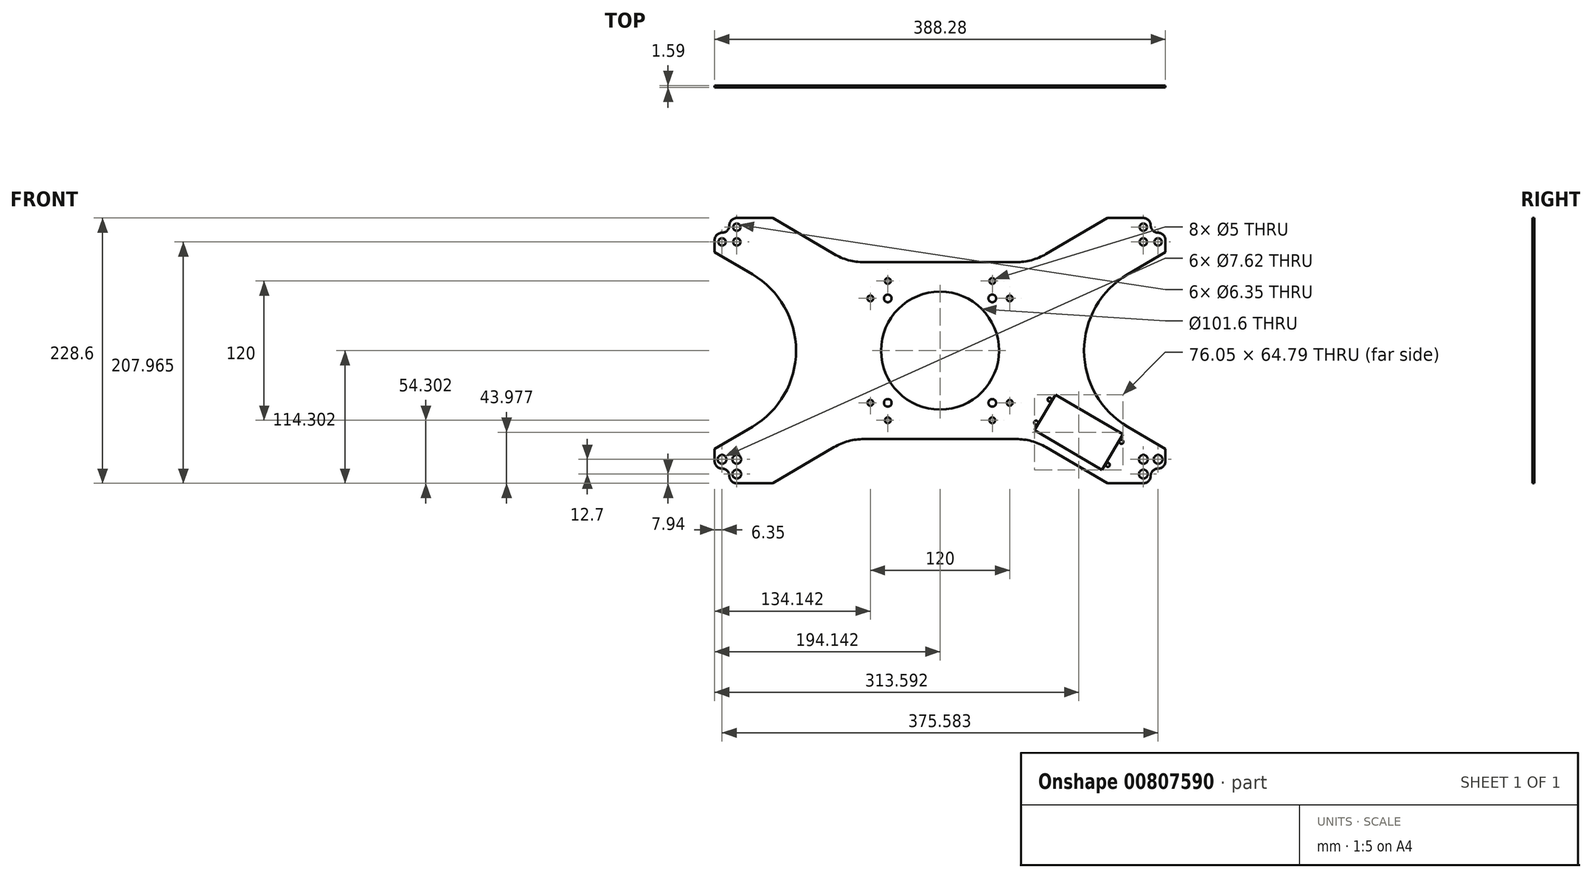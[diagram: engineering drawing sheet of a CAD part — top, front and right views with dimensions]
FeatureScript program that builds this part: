
annotation { "Feature Type Name" : "Feature", "Feature Type Description" : "" }
export const myFeature = defineFeature(function(context is Context, id is Id, definition is map)
    precondition{}
    {
        {
            var Q0;
            Q0=qCreatedBy(makeId("Front.planeOp"),FACE);
            var sketch = newSketch(context, id + "F0", { "sketchPlane" : qUnion([Q0])});
            skCircle(sketch, "E0", {"center": v(0, 0) * mm, "radius": 3.81 * mm});
            skCircle(sketch, "E1", {"center": v(0, 12.7) * mm, "radius": 3.81 * mm});
            skCircle(sketch, "E2", {"center": v(-12.7, 12.7) * mm, "radius": 3.81 * mm});
            skCircle(sketch, "E3", {"center": v(0, 200.03) * mm, "radius": 3.18 * mm});
            skCircle(sketch, "E4", {"center": v(0, 212.73) * mm, "radius": 3.18 * mm});
            skCircle(sketch, "E5", {"center": v(-12.7, 200.03) * mm, "radius": 3.18 * mm});
            skLineSegment(sketch, "E6", {"start": v(175.1, 263.95) * mm, "end": v(175.1, -51.23) * mm, "construction": true});
            skCircle(sketch, "E7.MirrorC", {"center": v(350.18, 212.73) * mm, "radius": 3.18 * mm});
            skCircle(sketch, "E8.MirrorC", {"center": v(362.88, 200.03) * mm, "radius": 3.18 * mm});
            skCircle(sketch, "E9.MirrorC", {"center": v(350.18, 12.7) * mm, "radius": 3.81 * mm});
            skCircle(sketch, "E10.MirrorC", {"center": v(362.88, 12.7) * mm, "radius": 3.81 * mm});
            skCircle(sketch, "E11.MirrorC", {"center": v(350.18, 200.03) * mm, "radius": 3.18 * mm});
            skCircle(sketch, "E12.MirrorC", {"center": v(350.18, 0) * mm, "radius": 3.81 * mm});
            skPoint(sketch, "E13", {"position": v(175.1, 106.36) * mm});
            skLineSegment(sketch, "E14", {"start": v(0, 200.03) * mm, "end": v(0, 12.7) * mm, "construction": true});
            skPoint(sketch, "E15", {"position": v(0, 106.36) * mm});
            skLineSegment(sketch, "E16.bottom", {"start": v(369.23, 220.66) * mm, "end": v(-19.05, 220.66) * mm, "construction": true});
            skLineSegment(sketch, "E16.top", {"start": v(369.23, -7.94) * mm, "end": v(-19.05, -7.94) * mm, "construction": true});
            skLineSegment(sketch, "E16.left", {"start": v(369.23, 220.66) * mm, "end": v(369.23, -7.94) * mm, "construction": true});
            skLineSegment(sketch, "E16.right", {"start": v(-19.05, 220.66) * mm, "end": v(-19.05, -7.94) * mm, "construction": true});
            skLineSegment(sketch, "E17.bottom", {"start": v(-19.05, 220.66) * mm, "end": v(-6.35, 220.66) * mm, "construction": true});
            skLineSegment(sketch, "E17.top", {"start": v(-19.05, 207.96) * mm, "end": v(-6.35, 207.96) * mm, "construction": true});
            skLineSegment(sketch, "E17.left", {"start": v(-19.05, 220.66) * mm, "end": v(-19.05, 207.96) * mm, "construction": true});
            skLineSegment(sketch, "E17.right", {"start": v(-6.35, 220.66) * mm, "end": v(-6.35, 207.96) * mm, "construction": true});
            skLineSegment(sketch, "E18", {"start": v(-19.05, 106.36) * mm, "end": v(369.23, 106.36) * mm, "construction": true});
            skLineSegment(sketch, "E19", {"start": v(31.01, 220.66) * mm, "end": v(175.1, 135.84) * mm, "construction": true});
            skLineSegment(sketch, "E20", {"start": v(-19.05, 191.19) * mm, "end": v(125.03, 106.36) * mm, "construction": true});
            skLineSegment(sketch, "E21", {"start": v(-19.05, 220.66) * mm, "end": v(175.1, 106.36) * mm, "construction": true});
            skLineSegment(sketch, "E22.MirrorCS", {"start": v(319.17, 220.66) * mm, "end": v(175.1, 135.84) * mm, "construction": true});
            skLineSegment(sketch, "E23.MirrorCS", {"start": v(369.23, 191.19) * mm, "end": v(225.16, 106.36) * mm, "construction": true});
            skLineSegment(sketch, "E24.MirrorCS", {"start": v(-19.05, 21.54) * mm, "end": v(125.03, 106.36) * mm, "construction": true});
            skLineSegment(sketch, "E25.MirrorCS", {"start": v(31.01, -7.94) * mm, "end": v(175.1, 76.89) * mm, "construction": true});
            skLineSegment(sketch, "E26.MirrorCS", {"start": v(319.17, -7.94) * mm, "end": v(175.1, 76.89) * mm, "construction": true});
            skLineSegment(sketch, "E27.MirrorCS", {"start": v(369.23, 21.54) * mm, "end": v(225.16, 106.36) * mm, "construction": true});
            skLineSegment(sketch, "E28.MirrorCS", {"start": v(369.23, 207.96) * mm, "end": v(356.53, 207.96) * mm, "construction": true});
            skLineSegment(sketch, "E29.MirrorCS", {"start": v(356.53, 220.66) * mm, "end": v(356.53, 207.96) * mm, "construction": true});
            skLineSegment(sketch, "E30.MirrorCS", {"start": v(-19.05, 4.76) * mm, "end": v(-6.35, 4.76) * mm, "construction": true});
            skLineSegment(sketch, "E31.MirrorCS", {"start": v(-6.35, -7.94) * mm, "end": v(-6.35, 4.76) * mm, "construction": true});
            skLineSegment(sketch, "E32.MirrorCS", {"start": v(356.53, -7.94) * mm, "end": v(356.53, 4.76) * mm, "construction": true});
            skLineSegment(sketch, "E33.MirrorCS", {"start": v(369.23, 4.76) * mm, "end": v(356.53, 4.76) * mm, "construction": true});
            skLineSegment(sketch, "E34", {"start": v(-19.05, 207.96) * mm, "end": v(-19.05, 191.19) * mm});
            skLineSegment(sketch, "E35", {"start": v(-19.05, 191.19) * mm, "end": v(13.5, 172.03) * mm});
            skLineSegment(sketch, "E36", {"start": v(-19.05, 21.54) * mm, "end": v(13.5, 40.7) * mm});
            skLineSegment(sketch, "E37", {"start": v(-19.05, 21.54) * mm, "end": v(-19.05, 4.76) * mm});
            skLineSegment(sketch, "E38", {"start": v(-6.35, 4.76) * mm, "end": v(-19.05, 4.76) * mm});
            skLineSegment(sketch, "E39", {"start": v(-6.35, 4.76) * mm, "end": v(-6.35, -7.94) * mm});
            skLineSegment(sketch, "E40", {"start": v(31.01, -7.94) * mm, "end": v(-6.35, -7.94) * mm});
            skLineSegment(sketch, "E41", {"start": v(31.01, -7.94) * mm, "end": v(83.8, 23.14) * mm});
            skLineSegment(sketch, "E42", {"start": v(266.38, 23.14) * mm, "end": v(319.17, -7.94) * mm});
            skLineSegment(sketch, "E43", {"start": v(319.17, -7.94) * mm, "end": v(356.53, -7.94) * mm});
            skLineSegment(sketch, "E44", {"start": v(356.53, -7.94) * mm, "end": v(356.53, 4.76) * mm});
            skLineSegment(sketch, "E45", {"start": v(356.53, 4.76) * mm, "end": v(369.23, 4.76) * mm});
            skLineSegment(sketch, "E46", {"start": v(369.23, 4.76) * mm, "end": v(369.23, 21.54) * mm});
            skLineSegment(sketch, "E47", {"start": v(369.23, 21.54) * mm, "end": v(336.69, 40.7) * mm});
            skLineSegment(sketch, "E48", {"start": v(336.69, 172.03) * mm, "end": v(369.23, 191.19) * mm});
            skLineSegment(sketch, "E49", {"start": v(369.23, 191.19) * mm, "end": v(369.23, 207.96) * mm});
            skLineSegment(sketch, "E50", {"start": v(369.23, 207.96) * mm, "end": v(356.53, 207.96) * mm});
            skLineSegment(sketch, "E51", {"start": v(356.53, 207.96) * mm, "end": v(356.53, 220.66) * mm});
            skLineSegment(sketch, "E52", {"start": v(356.53, 220.66) * mm, "end": v(319.17, 220.66) * mm});
            skLineSegment(sketch, "E53", {"start": v(319.17, 220.66) * mm, "end": v(266.38, 189.59) * mm});
            skLineSegment(sketch, "E54", {"start": v(-19.05, 207.96) * mm, "end": v(-6.35, 207.96) * mm});
            skLineSegment(sketch, "E55", {"start": v(-6.35, 207.96) * mm, "end": v(-6.35, 220.66) * mm});
            skLineSegment(sketch, "E56", {"start": v(-6.35, 220.66) * mm, "end": v(31.01, 220.66) * mm});
            skLineSegment(sketch, "E57", {"start": v(31.01, 220.66) * mm, "end": v(83.8, 189.59) * mm});
            skPoint(sketch, "E58.visualSharp", {"position": v(175.1, 135.84) * mm});
            skPoint(sketch, "E59.visualSharp", {"position": v(125.03, 106.36) * mm});
            skArc(sketch, "E59.filletArc", {"start": v(13.5, 40.7) * mm, "mid": v(51.03, 106.36) * mm, "end": v(13.5, 172.03) * mm});
            skPoint(sketch, "E60.visualSharp", {"position": v(175.1, 76.89) * mm});
            skPoint(sketch, "E61.visualSharp", {"position": v(225.16, 106.36) * mm});
            skArc(sketch, "E61.filletArc", {"start": v(336.69, 172.03) * mm, "mid": v(299.15, 106.36) * mm, "end": v(336.69, 40.7) * mm});
            skLineSegment(sketch, "E62.bottom", {"start": v(220.1, 151.36) * mm, "end": v(130.1, 151.36) * mm, "construction": true});
            skLineSegment(sketch, "E62.top", {"start": v(220.1, 61.36) * mm, "end": v(130.1, 61.36) * mm, "construction": true});
            skLineSegment(sketch, "E62.left", {"start": v(220.1, 151.36) * mm, "end": v(220.1, 61.36) * mm, "construction": true});
            skLineSegment(sketch, "E62.right", {"start": v(130.1, 151.36) * mm, "end": v(130.1, 61.36) * mm, "construction": true});
            skCircle(sketch, "E63", {"center": v(130.1, 151.36) * mm, "radius": 3.3 * mm});
            skCircle(sketch, "E64", {"center": v(220.1, 151.36) * mm, "radius": 3.3 * mm});
            skCircle(sketch, "E65", {"center": v(220.1, 61.36) * mm, "radius": 3.3 * mm});
            skCircle(sketch, "E66", {"center": v(130.1, 61.36) * mm, "radius": 3.3 * mm});
            skCircle(sketch, "E67", {"center": v(115.1, 151.36) * mm, "radius": 2.5 * mm});
            skCircle(sketch, "E68", {"center": v(130.1, 166.36) * mm, "radius": 2.5 * mm});
            skCircle(sketch, "E69.MirrorC", {"center": v(220.1, 166.36) * mm, "radius": 2.5 * mm});
            skCircle(sketch, "E70.MirrorC", {"center": v(235.1, 151.36) * mm, "radius": 2.5 * mm});
            skCircle(sketch, "E71.MirrorC", {"center": v(220.1, 46.36) * mm, "radius": 2.5 * mm});
            skCircle(sketch, "E72.MirrorC", {"center": v(235.1, 61.36) * mm, "radius": 2.5 * mm});
            skCircle(sketch, "E73.MirrorC", {"center": v(130.1, 46.36) * mm, "radius": 2.5 * mm});
            skCircle(sketch, "E74.MirrorC", {"center": v(115.1, 61.36) * mm, "radius": 2.5 * mm});
            skLineSegment(sketch, "E75", {"start": v(109.57, 182.56) * mm, "end": v(240.61, 182.56) * mm});
            skLineSegment(sketch, "E76", {"start": v(109.57, 30.16) * mm, "end": v(240.61, 30.16) * mm});
            skCircle(sketch, "E77", {"center": v(175.1, 106.36) * mm, "radius": 50.8 * mm});
            skPoint(sketch, "E78.visualSharp", {"position": v(95.73, 182.56) * mm});
            skArc(sketch, "E78.filletArc", {"start": v(83.8, 189.59) * mm, "mid": v(96.22, 184.35) * mm, "end": v(109.57, 182.56) * mm});
            skPoint(sketch, "E79.visualSharp", {"position": v(254.46, 182.56) * mm});
            skArc(sketch, "E79.filletArc", {"start": v(240.61, 182.56) * mm, "mid": v(253.97, 184.35) * mm, "end": v(266.38, 189.59) * mm});
            skPoint(sketch, "E80.visualSharp", {"position": v(95.73, 30.16) * mm});
            skArc(sketch, "E80.filletArc", {"start": v(109.57, 30.16) * mm, "mid": v(96.22, 28.38) * mm, "end": v(83.8, 23.14) * mm});
            skPoint(sketch, "E81.visualSharp", {"position": v(254.46, 30.16) * mm});
            skArc(sketch, "E81.filletArc", {"start": v(266.38, 23.14) * mm, "mid": v(253.97, 28.38) * mm, "end": v(240.61, 30.16) * mm});
            skLineSegment(sketch, "E82", {"start": v(-19.05, -7.94) * mm, "end": v(175.1, 106.36) * mm, "construction": true});
            skLineSegment(sketch, "E83", {"start": v(18.9, 27.75) * mm, "end": v(30.56, 7.93) * mm, "construction": true});
            skLineSegment(sketch, "E84", {"start": v(18.9, 27.75) * mm, "end": v(80.72, 64.15) * mm, "construction": true});
            skPoint(sketch, "E85", {"position": v(24.73, 17.84) * mm});
            skCircle(sketch, "E86", {"center": v(18.9, 27.75) * mm, "radius": 1.72 * mm, "construction": true});
            skCircle(sketch, "E87", {"center": v(80.72, 64.15) * mm, "radius": 1.72 * mm, "construction": true});
            skCircle(sketch, "E88", {"center": v(30.56, 7.93) * mm, "radius": 1.72 * mm, "construction": true});
            skLineSegment(sketch, "E89.bottom", {"start": v(35.66, 3.64) * mm, "end": v(93.66, 37.79) * mm, "construction": true});
            skLineSegment(sketch, "E89.top", {"start": v(17.62, 34.28) * mm, "end": v(75.62, 68.43) * mm, "construction": true});
            skLineSegment(sketch, "E89.left", {"start": v(35.66, 3.64) * mm, "end": v(17.62, 34.28) * mm, "construction": true});
            skLineSegment(sketch, "E89.right", {"start": v(93.66, 37.79) * mm, "end": v(75.62, 68.43) * mm, "construction": true});
            skPoint(sketch, "E89.middle", {"position": v(55.64, 36.04) * mm});
            skLineSegment(sketch, "E90", {"start": v(55.64, 36.04) * mm, "end": v(84.64, 53.11) * mm, "construction": true});
            skLineSegment(sketch, "E91", {"start": v(49.8, 45.95) * mm, "end": v(55.64, 36.04) * mm, "construction": true});
            skLineSegment(sketch, "E92.MirrorCS", {"start": v(256.52, 37.79) * mm, "end": v(274.56, 68.43) * mm});
            skCircle(sketch, "E93.MirrorC", {"center": v(269.46, 64.15) * mm, "radius": 1.72 * mm});
            skLineSegment(sketch, "E94.MirrorCS", {"start": v(332.56, 34.28) * mm, "end": v(274.56, 68.43) * mm});
            skLineSegment(sketch, "E95.MirrorCS", {"start": v(314.52, 3.64) * mm, "end": v(332.56, 34.28) * mm});
            skCircle(sketch, "E96.MirrorC", {"center": v(331.3, 27.75) * mm, "radius": 1.72 * mm});
            skCircle(sketch, "E97.MirrorC", {"center": v(319.62, 7.93) * mm, "radius": 1.72 * mm});
            skLineSegment(sketch, "E98.MirrorCS", {"start": v(314.52, 3.64) * mm, "end": v(256.52, 37.79) * mm});
            skCircle(sketch, "E99", {"center": v(257.8, 44.33) * mm, "radius": 1.72 * mm});
            skLineSegment(sketch, "E100", {"start": v(257.8, 44.33) * mm, "end": v(269.46, 64.15) * mm, "construction": true});
            skLineSegment(sketch, "E101", {"start": v(257.8, 44.33) * mm, "end": v(319.62, 7.93) * mm, "construction": true});
            skSolve(sketch);
        }
        {
            var Q0;
            Q0 = qSketchRegion(id + "F0", true);
            extrude(context, id + "F1", {"entities" : qUnion([Q0]), "depth" : 1.59 * mm, "offsetDistance" : 25.4 * mm});
        }
        {
            var Q0;
            Q0=makeQuery(id+"F1.opExtrude","SWEPT_EDGE",EDGE,{"disambiguationData":[OSD([sQuery(id+"F0.wireOp",EDGE,"E54"),sQuery(id+"F0.wireOp",EDGE,"E55")])]});
            var Q1;
            Q1=makeQuery(id+"F1.opExtrude","SWEPT_EDGE",EDGE,{"disambiguationData":[OSD([sQuery(id+"F0.wireOp",EDGE,"E55"),sQuery(id+"F0.wireOp",EDGE,"E56")])]});
            var Q2;
            Q2=makeQuery(id+"F1.opExtrude","SWEPT_EDGE",EDGE,{"disambiguationData":[OSD([sQuery(id+"F0.wireOp",EDGE,"E34"),sQuery(id+"F0.wireOp",EDGE,"E54")])]});
            var Q3;
            Q3=makeQuery(id+"F1.opExtrude","SWEPT_EDGE",EDGE,{"disambiguationData":[OSD([sQuery(id+"F0.wireOp",EDGE,"E50"),sQuery(id+"F0.wireOp",EDGE,"E51")])]});
            var Q4;
            Q4=makeQuery(id+"F1.opExtrude","SWEPT_EDGE",EDGE,{"disambiguationData":[OSD([sQuery(id+"F0.wireOp",EDGE,"E51"),sQuery(id+"F0.wireOp",EDGE,"E52")])]});
            var Q5;
            Q5=makeQuery(id+"F1.opExtrude","SWEPT_EDGE",EDGE,{"disambiguationData":[OSD([sQuery(id+"F0.wireOp",EDGE,"E49"),sQuery(id+"F0.wireOp",EDGE,"E50")])]});
            var Q6;
            Q6=makeQuery(id+"F1.opExtrude","SWEPT_EDGE",EDGE,{"disambiguationData":[OSD([sQuery(id+"F0.wireOp",EDGE,"E44"),sQuery(id+"F0.wireOp",EDGE,"E45")])]});
            var Q7;
            Q7=makeQuery(id+"F1.opExtrude","SWEPT_EDGE",EDGE,{"disambiguationData":[OSD([sQuery(id+"F0.wireOp",EDGE,"E45"),sQuery(id+"F0.wireOp",EDGE,"E46")])]});
            var Q8;
            Q8=makeQuery(id+"F1.opExtrude","SWEPT_EDGE",EDGE,{"disambiguationData":[OSD([sQuery(id+"F0.wireOp",EDGE,"E43"),sQuery(id+"F0.wireOp",EDGE,"E44")])]});
            var Q9;
            Q9=makeQuery(id+"F1.opExtrude","SWEPT_EDGE",EDGE,{"disambiguationData":[OSD([sQuery(id+"F0.wireOp",EDGE,"E38"),sQuery(id+"F0.wireOp",EDGE,"E39")])]});
            var Q10;
            Q10=makeQuery(id+"F1.opExtrude","SWEPT_EDGE",EDGE,{"disambiguationData":[OSD([sQuery(id+"F0.wireOp",EDGE,"E37"),sQuery(id+"F0.wireOp",EDGE,"E38")])]});
            var Q11;
            Q11=makeQuery(id+"F1.opExtrude","SWEPT_EDGE",EDGE,{"disambiguationData":[OSD([sQuery(id+"F0.wireOp",EDGE,"E39"),sQuery(id+"F0.wireOp",EDGE,"E40")])]});
            fillet(context, id + "F2", {"entities" : qUnion([Q0, Q1, Q2, Q3, Q4, Q5, Q6, Q7, Q8, Q9, Q10, Q11]), "tangentPropagation" : true, "radius" : 6.35 * mm, "defaultsChanged" : false, "vertexSettings" : [], "allowEdgeOverflow" : false});
        }
    });
